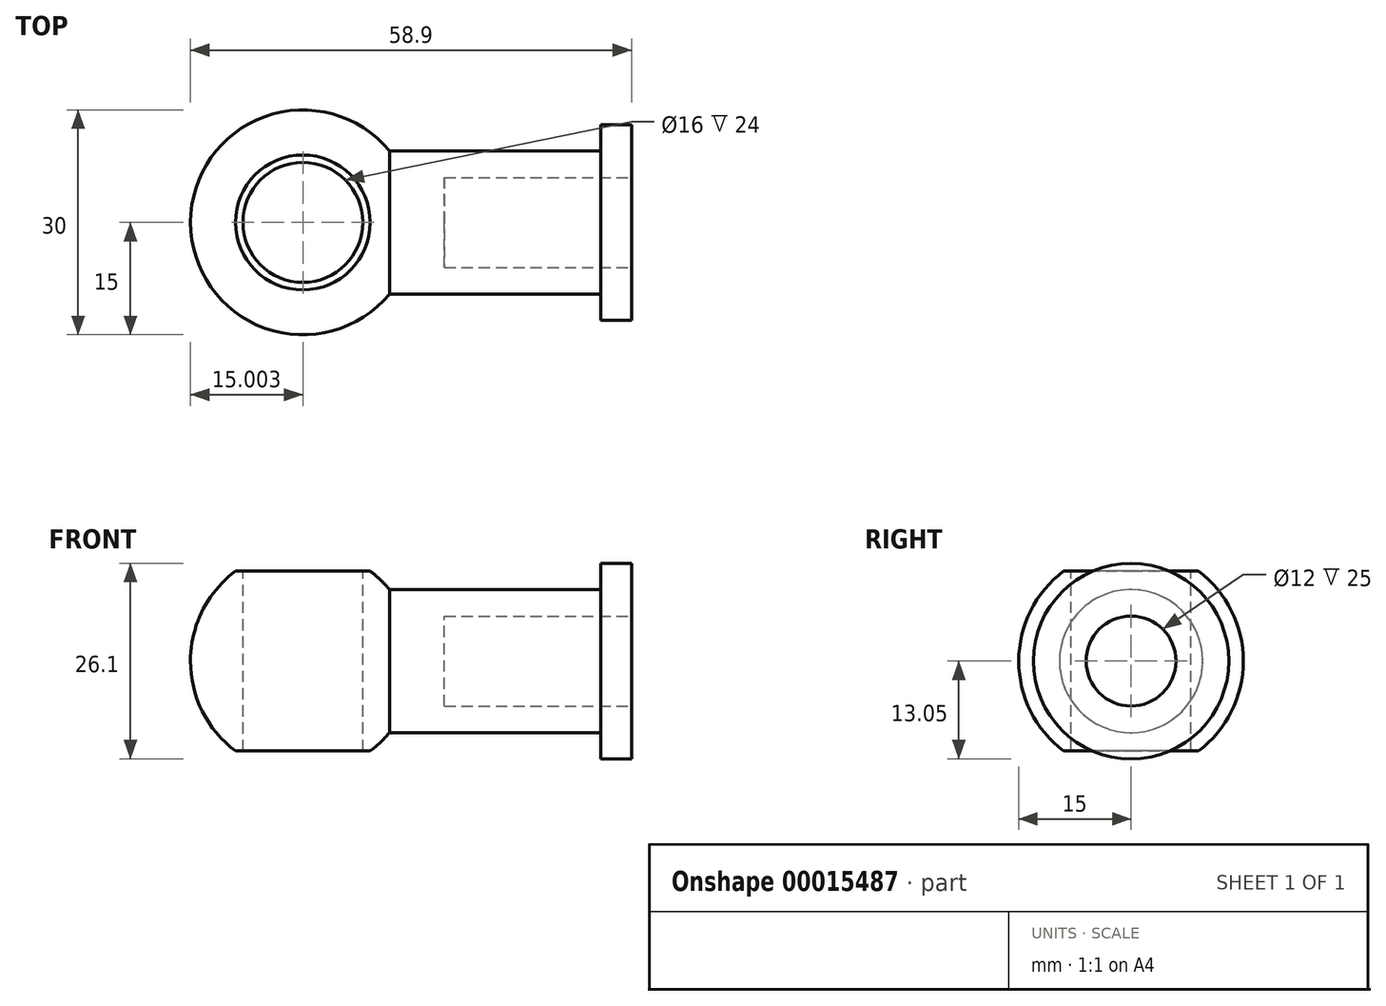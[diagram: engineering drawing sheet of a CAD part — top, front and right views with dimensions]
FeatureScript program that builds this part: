
annotation { "Feature Type Name" : "Feature", "Feature Type Description" : "" }
export const myFeature = defineFeature(function(context is Context, id is Id, definition is map)
    precondition{}
    {
        {
            var Q0;
            Q0=qCreatedBy(makeId("Front.planeOp"),FACE);
            var sketch = newSketch(context, id + "F0", { "sketchPlane" : qUnion([Q0])});
            skLineSegment(sketch, "E0", {"start": v(0, 0) * mm, "end": v(0, 13.05) * mm});
            skLineSegment(sketch, "E1", {"start": v(0, 13.05) * mm, "end": v(-4.1, 13.05) * mm});
            skLineSegment(sketch, "E2", {"start": v(-4.1, 13.05) * mm, "end": v(-4.1, 9.56) * mm});
            skLineSegment(sketch, "E3", {"start": v(-4.1, 9.56) * mm, "end": v(-32.33, 9.56) * mm});
            skArc(sketch, "E4", {"start": v(-32.33, 9.56) * mm, "mid": v(-48.97, 14.11) * mm, "end": v(-58.9, 0) * mm});
            skLineSegment(sketch, "E5", {"start": v(16.75, 0) * mm, "end": v(-76.68, 0) * mm});
            skSolve(sketch);
        }
        {
            var Q0;
            {var subQ2=sQuery(id+"F0.wireOp",EDGE,"E0");Q0=makeQuery(id+"F0.imprint","IMPRINT",FACE,{"disambiguationData":[TD([[makeQuery(id+"F0.imprint","IMPRINT",EDGE,{"derivedFrom":subQ2}),1.0]])]});}
            var Q1;
            Q1=sQuery(id+"F0.wireOp",EDGE,"E5");
            revolve(context, id + "F1", {"entities" : qUnion([Q0]), "axis" : qUnion([Q1]), "revolveType" : RevolveType.FULL});
        }
        {
            var Q0;
            Q0=qCreatedBy(makeId("Front.planeOp"),FACE);
            var sketch = newSketch(context, id + "F2", { "sketchPlane" : qUnion([Q0])});
            skLineSegment(sketch, "E6.bottom", {"start": v(-18.42, -12) * mm, "end": v(-54.23, -12) * mm});
            skLineSegment(sketch, "E6.top", {"start": v(-18.42, -26.02) * mm, "end": v(-54.23, -26.02) * mm});
            skLineSegment(sketch, "E6.left", {"start": v(-18.42, -12) * mm, "end": v(-18.42, -26.02) * mm});
            skLineSegment(sketch, "E6.right", {"start": v(-54.23, -12) * mm, "end": v(-54.23, -26.02) * mm});
            skLineSegment(sketch, "E7.bottom", {"start": v(-54.23, 12) * mm, "end": v(-20.44, 12) * mm});
            skLineSegment(sketch, "E7.top", {"start": v(-54.23, 20.46) * mm, "end": v(-20.44, 20.46) * mm});
            skLineSegment(sketch, "E7.left", {"start": v(-54.23, 12) * mm, "end": v(-54.23, 20.46) * mm});
            skLineSegment(sketch, "E7.right", {"start": v(-20.44, 12) * mm, "end": v(-20.44, 20.46) * mm});
            skSolve(sketch);
        }
        {
            var Q0;
            Q0=makeQuery(id+"F2.imprint","IMPRINT",FACE,{"disambiguationData":[TD([[makeQuery(id+"F2.imprint","IMPRINT",EDGE,{"derivedFrom":sQuery(id+"F2.wireOp",EDGE,"E7.bottom")}),1.0]])]});
            var Q1;
            Q1=makeQuery(id+"F2.imprint","IMPRINT",FACE,{"disambiguationData":[TD([[makeQuery(id+"F2.imprint","IMPRINT",EDGE,{"derivedFrom":sQuery(id+"F2.wireOp",EDGE,"E6.bottom")}),1.0]])]});
            extrude(context, id + "F3", {"entities" : qUnion([Q0, Q1]), "operationType" : NewBodyOperationType.REMOVE, "endBound" : BoundingType.SYMMETRIC, "oppositeDirection" : true, "depth" : 25 * mm});
        }
        {
            var Q0;
            Q0=makeQuery(id+"F3.boolean.opBoolean","COPY",FACE,{"derivedFrom":makeQuery(id+"F3.opExtrude","SWEPT_FACE",FACE,{"disambiguationData":[OSD([sQuery(id+"F2.wireOp",EDGE,"E7.bottom")])]})});
            var sketch = newSketch(context, id + "F4", { "sketchPlane" : qUnion([Q0])});
            skCircle(sketch, "E8", {"center": v(-43.9, 0) * mm, "radius": 8 * mm});
            skSolve(sketch);
        }
        {
            var Q0;
            Q0 = qSketchRegion(id + "F4", true);
            extrude(context, id + "F5", {"entities" : qUnion([Q0]), "operationType" : NewBodyOperationType.REMOVE, "oppositeDirection" : true, "depth" : 25 * mm});
        }
        {
            var Q0;
            Q0=makeQuery(id+"F1.opRevolve","SWEPT_FACE",FACE,{"disambiguationData":[OSD([sQuery(id+"F0.wireOp",EDGE,"E0")])]});
            var sketch = newSketch(context, id + "F6", { "sketchPlane" : qUnion([Q0])});
            skCircle(sketch, "E9", {"center": v(0, 0) * mm, "radius": 6 * mm});
            skSolve(sketch);
        }
        {
            var Q0;
            Q0 = qSketchRegion(id + "F6", true);
            extrude(context, id + "F7", {"entities" : qUnion([Q0]), "operationType" : NewBodyOperationType.REMOVE, "oppositeDirection" : true, "depth" : 25 * mm});
        }
    });
